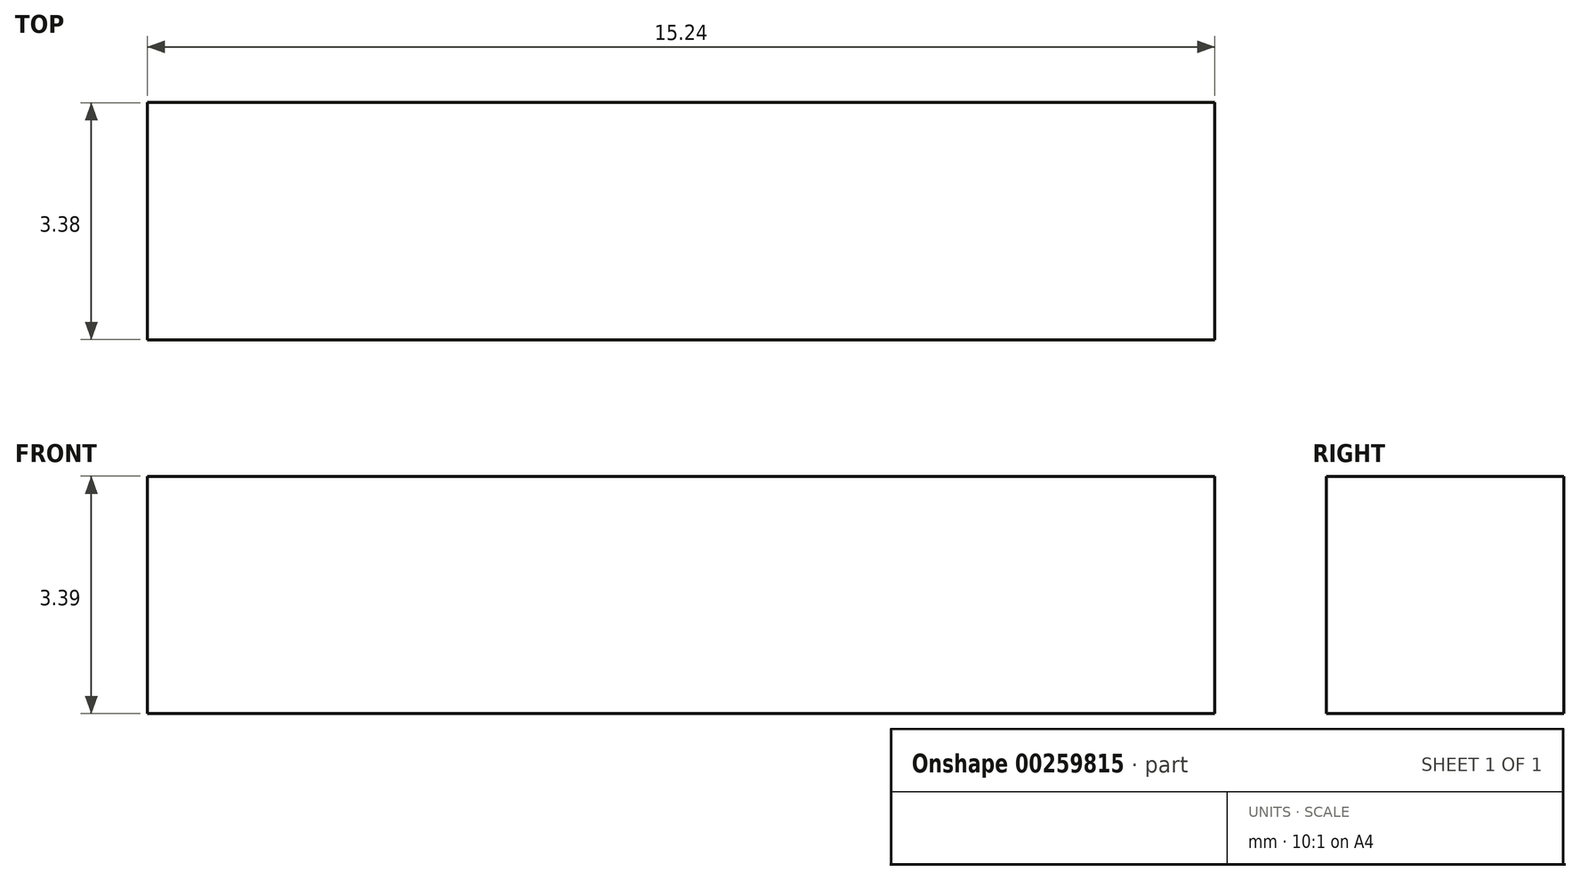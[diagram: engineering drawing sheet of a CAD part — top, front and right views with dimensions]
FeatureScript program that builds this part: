
annotation { "Feature Type Name" : "Feature", "Feature Type Description" : "" }
export const myFeature = defineFeature(function(context is Context, id is Id, definition is map)
    precondition{}
    {
        {
            var Q0;
            Q0=qCreatedBy(makeId("Top.planeOp"),FACE);
            var sketch = newSketch(context, id + "F0", { "sketchPlane" : qUnion([Q0])});
            skLineSegment(sketch, "E0.bottom", {"start": v(7.62, -1.7) * mm, "end": v(-7.62, -1.7) * mm});
            skLineSegment(sketch, "E0.top", {"start": v(7.62, 1.7) * mm, "end": v(-7.62, 1.7) * mm});
            skLineSegment(sketch, "E0.left", {"start": v(7.62, -1.7) * mm, "end": v(7.62, 1.7) * mm});
            skLineSegment(sketch, "E0.right", {"start": v(-7.62, -1.7) * mm, "end": v(-7.62, 1.7) * mm});
            skPoint(sketch, "E0.middle", {"position": v(0, 0) * mm});
            skSolve(sketch);
        }
        {
            var Q0;
            Q0 = qSketchRegion(id + "F0", true);
            extrude(context, id + "F1", {"entities" : qUnion([Q0]), "depth" : 3.4 * mm});
        }
    });
